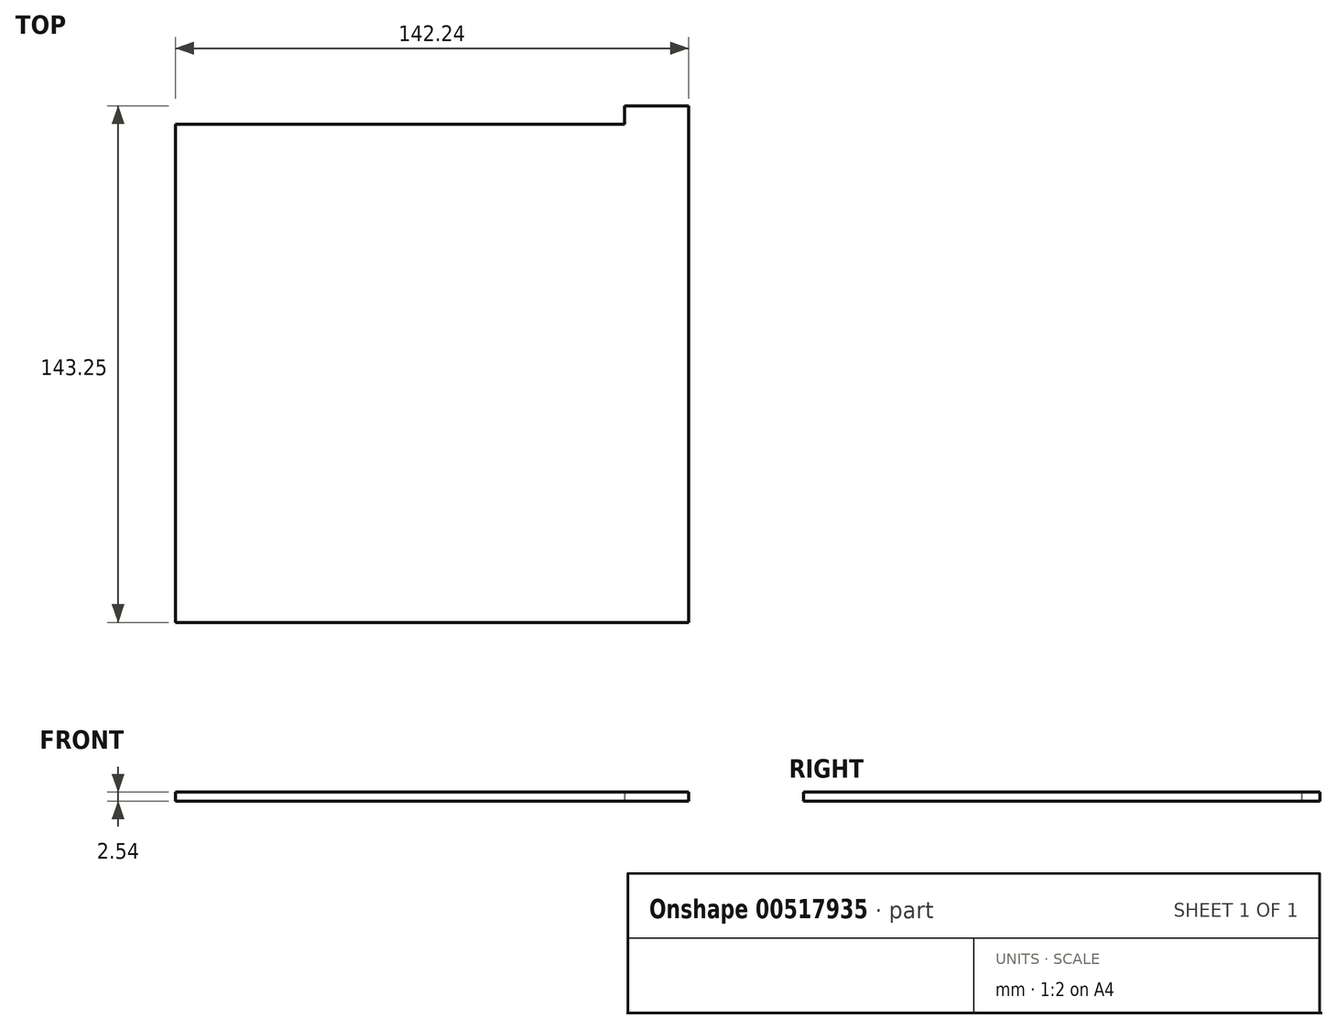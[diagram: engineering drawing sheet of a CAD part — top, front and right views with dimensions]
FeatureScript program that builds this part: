
annotation { "Feature Type Name" : "Feature", "Feature Type Description" : "" }
export const myFeature = defineFeature(function(context is Context, id is Id, definition is map)
    precondition{}
    {
        {
            var Q0;
            Q0=qCreatedBy(makeId("Top.planeOp"),FACE);
            var sketch = newSketch(context, id + "F0", { "sketchPlane" : qUnion([Q0])});
            skLineSegment(sketch, "E0", {"start": v(-81.3, 104.01) * mm, "end": v(60.95, 104.01) * mm});
            skLineSegment(sketch, "E1", {"start": v(60.95, 104.01) * mm, "end": v(60.95, -34.16) * mm});
            skLineSegment(sketch, "E2", {"start": v(60.95, -34.16) * mm, "end": v(-81.3, -34.16) * mm});
            skLineSegment(sketch, "E3", {"start": v(-81.3, -34.16) * mm, "end": v(-81.3, 104.01) * mm});
            skLineSegment(sketch, "E4", {"start": v(43.17, 104.01) * mm, "end": v(43.17, 109.1) * mm});
            skLineSegment(sketch, "E5", {"start": v(43.17, 109.1) * mm, "end": v(60.95, 109.1) * mm});
            skLineSegment(sketch, "E6", {"start": v(60.95, 109.1) * mm, "end": v(60.95, 104.01) * mm});
            skSolve(sketch);
        }
        {
            var Q0;
            Q0=makeQuery(id+"F0.imprint","IMPRINT",FACE,{"disambiguationData":[TD([[makeQuery(id+"F0.imprint","IMPRINT",EDGE,{"derivedFrom":sQuery(id+"F0.wireOp",EDGE,"E0")}),-1.0]])]});
            extrude(context, id + "F1", {"entities" : qUnion([Q0]), "depth" : 2.54 * mm, "offsetDistance" : 25.4 * mm});
        }
        {
            var Q0;
            {var subQ2=sQuery(id+"F0.wireOp",EDGE,"E4");Q0=makeQuery(id+"F0.imprint","IMPRINT",FACE,{"disambiguationData":[TD([[makeQuery(id+"F0.imprint","IMPRINT",EDGE,{"derivedFrom":subQ2}),-1.0]])]});}
            extrude(context, id + "F2", {"entities" : qUnion([Q0]), "operationType" : NewBodyOperationType.ADD, "depth" : 2.54 * mm, "offsetDistance" : 25.4 * mm});
        }
    });
